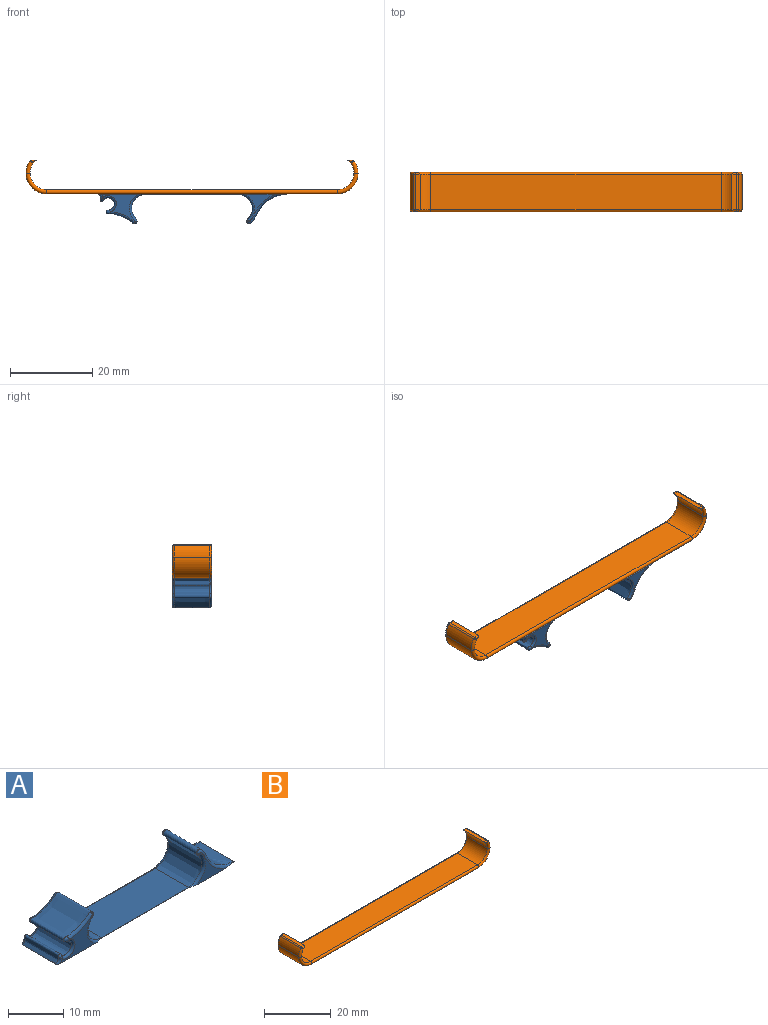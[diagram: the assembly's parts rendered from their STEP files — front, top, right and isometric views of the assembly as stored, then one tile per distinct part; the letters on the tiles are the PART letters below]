
ASSEMBLY  parts=2 mates=1
PART A: 36 faces, bbox 46.2x9.5x7.7 mm
  f0: plane 9.01x6.68mm, normal (0,-1,0), area 22.1mm2, adj f7,f23,f25,f27,f29,f31
  f1: plane 9.01x6.68mm, normal (0,1,0), area 22.1mm2, adj f7,f10,f12,f14,f16,f18
  f2: plane 22.42x8.53mm, normal (0,0,1), area 191.1mm2, adj f8,f9,f19,f32
  f3: plane 7.25x6.66mm, normal (0,1,0), area 11.6mm2, adj f7,f20,f21
  f4: plane 8.72x0.01mm, normal (1,0,0), area 0.1mm2, adj f7,f9,f20,f33
  f5: plane 7.25x6.66mm, normal (0,-1,0), area 11.6mm2, adj f7,f33,f34
  f6: plane 8.7x0.01mm, normal (-1,0,0), area 0.1mm2, adj f7,f8,f10,f23
  f7: plane 45.72x9.53mm, normal (0,0,-1), area 415.4mm2, adj f0,f1,f3,f4,f5,f6,f10,f18
  f8: extruded ~11.64x8.53mm, area 229mm2, adj f2,f6,f10,f11,f12,f13,f14,f15
  f9: extruded ~11.66x8.53mm, area 187mm2, adj f2,f4,f20,f21,f22,f33,f34,f35
  f10: bspline ~1.95x1.33mm, area 1mm2, adj f1,f6,f7,f8,f11
  f11: bspline ~0.9x0.69mm, area 0.5mm2, adj f8,f10,f12
  f12: bspline ~3.96x3.62mm, area 4.9mm2, adj f1,f8,f11,f13
  f13: bspline ~1.13x0.95mm, area 1.3mm2, adj f8,f12,f14
  f14: bspline ~6.72x2.94mm, area 5.1mm2, adj f1,f8,f13,f15
  f15: bspline ~0.5x0.5mm, area 0.2mm2, adj f8,f14,f16
  f16: bspline ~0.67x0.65mm, area 0.2mm2, adj f1,f8,f15,f17
  f17: bspline ~0.5x0.5mm, area 0.1mm2, adj f8,f16,f18
  f18: bspline ~7.32x4.08mm, area 6.5mm2, adj f1,f7,f8,f17,f19
  f19: cylinder r=0.5mm len=22.42mm, axis (-1,0,0), area 2.2mm2, adj f2,f7,f18,f21
  f20: bspline ~9.92x7.7mm, area 9.2mm2, adj f3,f4,f7,f9,f22
  f21: bspline ~7.12x6.74mm, area 6.3mm2, adj f3,f7,f9,f19,f22
  f22: bspline ~0.5x0.5mm, area 0.1mm2, adj f9,f20,f21
  f23: bspline ~1.95x1.33mm, area 1mm2, adj f0,f6,f7,f8,f24
  f24: bspline ~0.9x0.69mm, area 0.4mm2, adj f8,f23,f25
  f25: bspline ~3.96x3.62mm, area 4.9mm2, adj f0,f8,f24,f26
  f26: bspline ~1.13x0.95mm, area 1.3mm2, adj f8,f25,f27
  f27: bspline ~6.45x2.94mm, area 5.1mm2, adj f0,f8,f26,f28
  f28: bspline ~0.5x0.5mm, area 0.2mm2, adj f8,f27,f29
  f29: bspline ~0.62x0.6mm, area 0.2mm2, adj f0,f8,f28,f30
  f30: bspline ~0.5x0.5mm, area 0.1mm2, adj f8,f29,f31
  f31: bspline ~7.16x4.08mm, area 6.5mm2, adj f0,f7,f8,f30,f32
  f32: cylinder r=0.5mm len=22.42mm, axis (1,0,0), area 2.2mm2, adj f2,f7,f31,f34
  f33: bspline ~9.86x7.69mm, area 9.2mm2, adj f4,f5,f7,f9,f35
  f34: bspline ~7.12x6.74mm, area 6.3mm2, adj f5,f7,f9,f32,f35
  f35: bspline ~0.5x0.5mm, area 0.1mm2, adj f9,f33,f34
PART B: 42 faces, bbox 81.6x9.5x9.7 mm
  f0: plane 8.57x0mm, normal (-0.77,0,0.64), area 0mm2, adj f15,f17,f35,f36,f37,f38
  f1: plane 8.57x0mm, normal (0.77,0,0.64), area 0mm2, adj f9,f16,f18,f20,f21,f24
  f2: cylinder r=5.04mm len=8.53mm, axis (0,-1,0), area 26.2mm2, adj f3,f19,f21,f24
  f3: plane 8.53x0.02mm, normal (-1,0,0), area 0.2mm2, adj f2,f4,f25,f26
  f4: cylinder r=5.04mm len=8.53mm, axis (0,-1,0), area 67.5mm2, adj f3,f5,f27,f28
  f5: plane 70.66x8.53mm, normal (0,0,-1), area 602.4mm2, adj f4,f6,f29,f30
  f6: cylinder r=5.04mm len=8.53mm, axis (0,-1,0), area 67.5mm2, adj f5,f7,f31,f32
  f7: plane 8.53x0.02mm, normal (1,0,0), area 0.2mm2, adj f6,f8,f33,f34
  f8: cylinder r=5.04mm len=8.53mm, axis (0,-1,0), area 26.2mm2, adj f7,f35,f36,f41
  f9: cylinder r=4.04mm len=8.53mm, axis (0,-1,0), area 30.3mm2, adj f1,f10,f21,f24
  f10: plane 8.53x0.02mm, normal (1,0,0), area 0.2mm2, adj f9,f11,f25,f26
  f11: cylinder r=4.04mm len=8.53mm, axis (0,-1,0), area 54.1mm2, adj f10,f12,f27,f28
  f12: plane 70.66x8.53mm, normal (0,0,1), area 602.4mm2, adj f11,f13,f29,f30
  f13: cylinder r=4.04mm len=8.53mm, axis (0,-1,0), area 54.1mm2, adj f12,f14,f31,f32
  f14: plane 8.53x0.02mm, normal (-1,0,0), area 0.2mm2, adj f13,f15,f33,f34
  f15: cylinder r=4.04mm len=8.53mm, axis (0,-1,0), area 30.3mm2, adj f0,f14,f35,f36
  f16: plane 8.53x1.16mm, normal (-0.01,0,1), area 9.9mm2, adj f1,f18,f19,f20
  f17: plane 8.53x1.16mm, normal (0.01,0,1), area 9.9mm2, adj f0,f37,f38,f41
  f18: cylinder r=0.5mm len=1.16mm, axis (-1,0,-0.01), area 0.6mm2, adj f1,f16,f21,f22
  f19: cylinder r=0.5mm len=8.53mm, axis (0,-1,0), area 4mm2, adj f2,f16,f22,f23
  f20: cylinder r=0.5mm len=1.16mm, axis (-1,0,-0.01), area 0.6mm2, adj f1,f16,f23,f24
  f21: torus R=4.54mm, axis (0,1,0), area 4.9mm2, adj f1,f2,f9,f18,f22,f25
  f22: sphere r=0.5mm, area 0.2mm2, adj f18,f19,f21
  f23: sphere r=0.5mm, area 0.2mm2, adj f19,f20,f24
  f24: torus R=4.54mm, axis (0,1,0), area 4.9mm2, adj f1,f2,f9,f20,f23,f26
  f25: cylinder r=0.5mm len=1mm, axis (0,0,1), area 0mm2, adj f3,f10,f21,f27
  f26: cylinder r=0.5mm len=1mm, axis (0,0,-1), area 0mm2, adj f3,f10,f24,f28
  f27: torus R=4.54mm, axis (0,1,0), area 11.2mm2, adj f4,f11,f25,f29
  f28: torus R=4.54mm, axis (0,1,0), area 11.2mm2, adj f4,f11,f26,f30
  f29: cylinder r=0.5mm len=70.66mm, axis (-1,0,0), area 111mm2, adj f5,f12,f27,f31
  f30: cylinder r=0.5mm len=70.66mm, axis (1,0,0), area 111mm2, adj f5,f12,f28,f32
  f31: torus R=4.54mm, axis (0,1,0), area 11.2mm2, adj f6,f13,f29,f33
  f32: torus R=4.54mm, axis (0,1,0), area 11.2mm2, adj f6,f13,f30,f34
  f33: cylinder r=0.5mm len=1mm, axis (0,0,-1), area 0mm2, adj f7,f14,f31,f35
  f34: cylinder r=0.5mm len=1mm, axis (0,0,1), area 0mm2, adj f7,f14,f32,f36
  f35: torus R=4.54mm, axis (0,1,0), area 4.9mm2, adj f0,f8,f15,f33,f37,f39
  f36: torus R=4.54mm, axis (0,1,0), area 4.9mm2, adj f0,f8,f15,f34,f38,f40
  f37: cylinder r=0.5mm len=1.16mm, axis (-1,0,0.01), area 0.6mm2, adj f0,f17,f35,f39
  f38: cylinder r=0.5mm len=1.16mm, axis (-1,0,0.01), area 0.6mm2, adj f0,f17,f36,f40
  f39: sphere r=0.5mm, area 0.2mm2, adj f35,f37,f41
  f40: sphere r=0.5mm, area 0.2mm2, adj f36,f38,f41
  f41: cylinder r=0.5mm len=8.53mm, axis (0,-1,0), area 4mm2, adj f8,f17,f39,f40
PLACE A rot(axis=(1,0,0),180deg) t=(-0.42,-11.11,-4.48)mm
PLACE B t=(-0.29,-1.59,0)mm
MATE slider A.f7 <-> B.f5  axis (0,0,1) through (-0.29,-6.35,-1.49)mm
